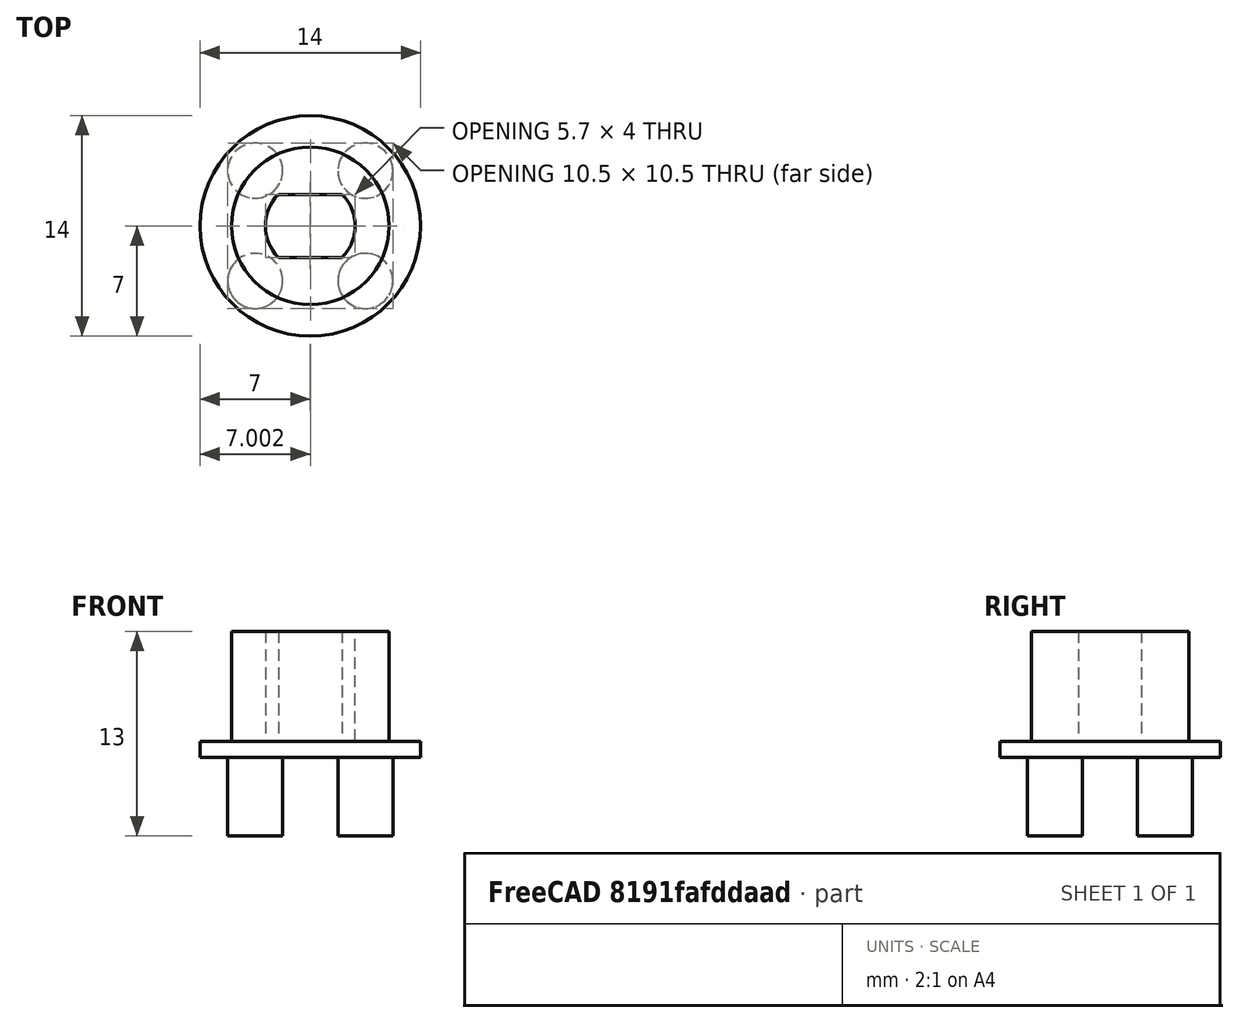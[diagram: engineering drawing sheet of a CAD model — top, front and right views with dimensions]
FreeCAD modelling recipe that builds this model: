
FCSTD DOCUMENT  (FreeCAD 0.20R29177 +426 (Git))
Label: reductorAdapter
License: All rights reserved
LicenseURL: http://en.wikipedia.org/wiki/All_rights_reserved
objects: Part::Cylinder×7, Part::MultiFuse×3, Part::Box×1, Part::MultiCommon×1, Part::Cut×1, Mesh::Feature×1
note: 13 computed .brp shape members not serialized (recipe doc carries the construction recipe); baked Part::Feature solids carry a one-line shape summary decoded from their .brp

FEATURE [Part::Cylinder] Cylinder
  Angle = 360
  AttacherType = Attacher::AttachEngine3D
  FirstAngle = 0
  Height = 10
  Radius = 2.85
  SecondAngle = 0
FEATURE [Part::Box] Box  label="Cube"
  AttacherType = Attacher::AttachEngine3D
  Height = 10
  Length = 8
  Placement = pos=(-4,-2,0) rot=(0,0,1;0rad)
  Width = 4
FEATURE [Part::MultiCommon] Common
  Shapes = -> [Cylinder,Box]
FEATURE [Part::Cylinder] Cylinder001
  Angle = 360
  AttacherType = Attacher::AttachEngine3D
  FirstAngle = 0
  Height = 1
  Radius = 7
  SecondAngle = 0
FEATURE [Part::Cylinder] Cylinder002
  Angle = 360
  AttacherType = Attacher::AttachEngine3D
  FirstAngle = 0
  Height = 8
  Radius = 5
  SecondAngle = 0
FEATURE [Part::Cut] Cut
  Base = -> Cylinder002
  Tool = -> Common
FEATURE [Part::Cylinder] Cylinder003
  Angle = 360
  AttacherType = Attacher::AttachEngine3D
  FirstAngle = 0
  Height = 6
  Placement = pos=(-3.5,-3.5,-5) rot=(0,0,1;0rad)
  Radius = 1.75
  SecondAngle = 0
FEATURE [Part::Cylinder] Cylinder004
  Angle = 360
  AttacherType = Attacher::AttachEngine3D
  FirstAngle = 0
  Height = 6
  Placement = pos=(3.5,3.5,-5) rot=(0,0,1;0rad)
  Radius = 1.75
  SecondAngle = 0
FEATURE [Part::Cylinder] Cylinder005
  Angle = 360
  AttacherType = Attacher::AttachEngine3D
  FirstAngle = 0
  Height = 6
  Placement = pos=(3.5,-3.5,-5) rot=(0,0,1;0rad)
  Radius = 1.75
  SecondAngle = 0
FEATURE [Part::Cylinder] Cylinder006
  Angle = 360
  AttacherType = Attacher::AttachEngine3D
  FirstAngle = 0
  Height = 6
  Placement = pos=(-3.5,3.5,-5) rot=(0,0,1;0rad)
  Radius = 1.75
  SecondAngle = 0
FEATURE [Part::MultiFuse] Fusion
  Shapes = -> [Cylinder003,Cylinder004,Cylinder005,Cylinder006]
FEATURE [Part::MultiFuse] Fusion001
  Shapes = -> [Cylinder001,Fusion]
FEATURE [Part::MultiFuse] Fusion002
  Shapes = -> [Cut,Fusion001]
FEATURE [Mesh::Feature] Mesh  label="Fusion002 (Meshed)"
